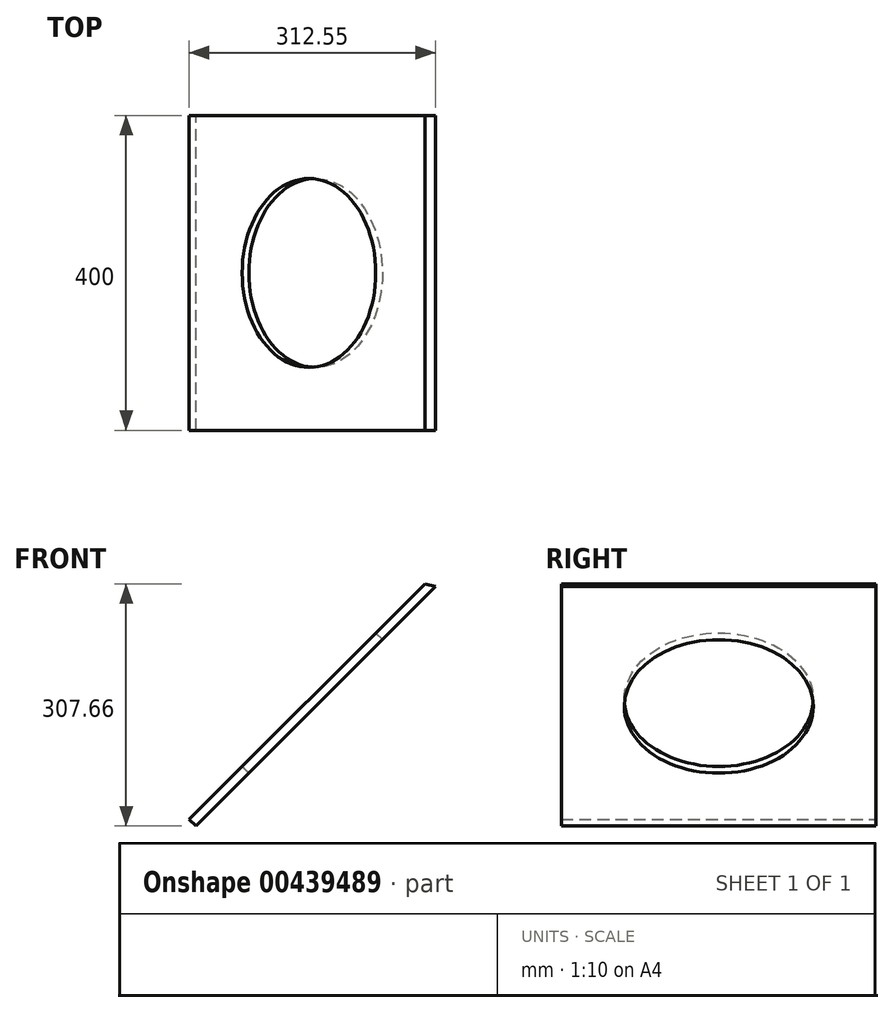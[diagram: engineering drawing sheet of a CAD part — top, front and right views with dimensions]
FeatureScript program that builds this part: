
annotation { "Feature Type Name" : "Feature", "Feature Type Description" : "" }
export const myFeature = defineFeature(function(context is Context, id is Id, definition is map)
    precondition{}
    {
        {
            var Q0;
            Q0=qCreatedBy(makeId("Front.planeOp"),FACE);
            var sketch = newSketch(context, id + "F0", { "sketchPlane" : qUnion([Q0])});
            skLineSegment(sketch, "E0", {"start": v(127.44, -185) * mm, "end": v(-278.86, -185) * mm, "construction": true});
            skLineSegment(sketch, "E1", {"start": v(-278.86, -185) * mm, "end": v(-278.86, 66.39) * mm, "construction": true});
            skLineSegment(sketch, "E2", {"start": v(-274.47, 77) * mm, "end": v(19.17, 370.63) * mm, "construction": true});
            skLineSegment(sketch, "E3", {"start": v(28.83, 373.21) * mm, "end": v(116.32, 349.77) * mm, "construction": true});
            skLineSegment(sketch, "E4", {"start": v(127.44, 335.28) * mm, "end": v(127.44, -185) * mm, "construction": true});
            skLineSegment(sketch, "E5", {"start": v(-273.86, -175) * mm, "end": v(-273.86, 61.28) * mm, "construction": true});
            skLineSegment(sketch, "E6", {"start": v(-278.86, 63.36) * mm, "end": v(25.2, 367.42) * mm, "construction": true});
            skLineSegment(sketch, "E7", {"start": v(25.2, 367.42) * mm, "end": v(120.9, 341.78) * mm, "construction": true});
            skLineSegment(sketch, "E8", {"start": v(112, 331.74) * mm, "end": v(112, -55) * mm, "construction": true});
            skLineSegment(sketch, "E9", {"start": v(100, -167) * mm, "end": v(-261.86, -167) * mm, "construction": true});
            skLineSegment(sketch, "E10", {"start": v(100, -167) * mm, "end": v(100, -185) * mm, "construction": true});
            skLineSegment(sketch, "E11", {"start": v(-261.86, -167) * mm, "end": v(-261.86, -175) * mm, "construction": true});
            skLineSegment(sketch, "E12", {"start": v(-261.86, -175) * mm, "end": v(-273.86, -175) * mm, "construction": true});
            skLineSegment(sketch, "E13", {"start": v(120.9, 341.78) * mm, "end": v(117.8, 330.19) * mm, "construction": true});
            skLineSegment(sketch, "E14", {"start": v(117.8, 330.19) * mm, "end": v(112, 331.74) * mm, "construction": true});
            skLineSegment(sketch, "E15", {"start": v(-273.86, 61.28) * mm, "end": v(20.98, 356.13) * mm, "construction": true});
            skLineSegment(sketch, "E16", {"start": v(112, 331.74) * mm, "end": v(15.4, 357.62) * mm});
            skPoint(sketch, "E17.visualSharp", {"position": v(-278.86, 72.6) * mm});
            skArc(sketch, "E17.filletArc", {"start": v(-274.47, 77) * mm, "mid": v(-277.72, 72.13) * mm, "end": v(-278.86, 66.39) * mm, "construction": true});
            skPoint(sketch, "E18.visualSharp", {"position": v(23.25, 374.7) * mm});
            skArc(sketch, "E18.filletArc", {"start": v(28.83, 373.21) * mm, "mid": v(23.65, 373.21) * mm, "end": v(19.17, 370.63) * mm, "construction": true});
            skPoint(sketch, "E19.visualSharp", {"position": v(127.44, 346.8) * mm});
            skArc(sketch, "E19.filletArc", {"start": v(127.44, 335.28) * mm, "mid": v(124.34, 344.41) * mm, "end": v(116.32, 349.77) * mm, "construction": true});
            skLineSegment(sketch, "E20", {"start": v(23.65, 373.21) * mm, "end": v(26.24, 363.56) * mm, "construction": true});
            skLineSegment(sketch, "E21.left", {"start": v(50, 24) * mm, "end": v(50, 70) * mm, "construction": true});
            skLineSegment(sketch, "E21.right", {"start": v(-50, 24) * mm, "end": v(-50, 70) * mm, "construction": true});
            skPoint(sketch, "E21.middle", {"position": v(0, 0) * mm});
            skArc(sketch, "E22.filletArc", {"start": v(-35, 85) * mm, "mid": v(-45.6, 80.6) * mm, "end": v(-50, 70) * mm, "construction": true});
            skArc(sketch, "E23.filletArc", {"start": v(50, 70) * mm, "mid": v(45.6, 80.6) * mm, "end": v(35, 85) * mm, "construction": true});
            skLineSegment(sketch, "E24", {"start": v(-261.86, 73.28) * mm, "end": v(-233.57, 45) * mm, "construction": true});
            skLineSegment(sketch, "E25", {"start": v(-233.57, 45) * mm, "end": v(65.6, 344.17) * mm});
            skLineSegment(sketch, "E26", {"start": v(112.44, 335.28) * mm, "end": v(124.34, 344.41) * mm, "construction": true});
            skLineSegment(sketch, "E27", {"start": v(100, -155) * mm, "end": v(100, -67) * mm, "construction": true});
            skLineSegment(sketch, "E28", {"start": v(100, -55) * mm, "end": v(88, -55) * mm, "construction": true});
            skLineSegment(sketch, "E29", {"start": v(88, -55) * mm, "end": v(88, -155) * mm, "construction": true});
            skLineSegment(sketch, "E30", {"start": v(88, -155) * mm, "end": v(100, -155) * mm, "construction": true});
            skLineSegment(sketch, "E31", {"start": v(100, -55) * mm, "end": v(100, 334.95) * mm, "construction": true});
            skLineSegment(sketch, "E32", {"start": v(-82, -155) * mm, "end": v(-261.86, -155) * mm, "construction": true});
            skLineSegment(sketch, "E33", {"start": v(-82, -155) * mm, "end": v(88, -155) * mm, "construction": true});
            skLineSegment(sketch, "E34", {"start": v(-82, -155) * mm, "end": v(-82, 25) * mm, "construction": true});
            skLineSegment(sketch, "E35", {"start": v(88, 25) * mm, "end": v(-82, 25) * mm, "construction": true});
            skLineSegment(sketch, "E36", {"start": v(88, -55) * mm, "end": v(88, 25) * mm, "construction": true});
            skLineSegment(sketch, "E37", {"start": v(-50, 24) * mm, "end": v(-55, 24) * mm, "construction": true});
            skLineSegment(sketch, "E38", {"start": v(55, 24) * mm, "end": v(50, 24) * mm, "construction": true});
            skLineSegment(sketch, "E39", {"start": v(-55, 24) * mm, "end": v(-55, 194) * mm, "construction": true});
            skLineSegment(sketch, "E40", {"start": v(55, 194) * mm, "end": v(55, 24) * mm, "construction": true});
            skLineSegment(sketch, "E41", {"start": v(127.44, -55) * mm, "end": v(-261.86, -55) * mm, "construction": true});
            skLineSegment(sketch, "E42", {"start": v(-261.86, -55) * mm, "end": v(-261.86, -67) * mm, "construction": true});
            skLineSegment(sketch, "E43", {"start": v(-261.86, -67) * mm, "end": v(88, -67) * mm, "construction": true});
            skLineSegment(sketch, "E44", {"start": v(127.44, -67) * mm, "end": v(127.44, -55) * mm});
            skLineSegment(sketch, "E45", {"start": v(100, -67) * mm, "end": v(100, -55) * mm, "construction": true});
            skLineSegment(sketch, "E46", {"start": v(88, -67) * mm, "end": v(127.44, -67) * mm, "construction": true});
            skLineSegment(sketch, "E47", {"start": v(112, -67) * mm, "end": v(112, -185) * mm, "construction": true});
            skLineSegment(sketch, "E48", {"start": v(112, -55) * mm, "end": v(112, -67) * mm, "construction": true});
            skLineSegment(sketch, "E49", {"start": v(-261.86, -55) * mm, "end": v(-261.86, -55) * mm});
            skLineSegment(sketch, "E50", {"start": v(-261.86, -55) * mm, "end": v(-261.86, 73.28) * mm, "construction": true});
            skLineSegment(sketch, "E51", {"start": v(-273.86, 61.28) * mm, "end": v(-278.86, 56.28) * mm, "construction": true});
            skLineSegment(sketch, "E52", {"start": v(-233.57, 45) * mm, "end": v(-225.09, 36.51) * mm});
            skLineSegment(sketch, "E53", {"start": v(-225.09, 36.51) * mm, "end": v(78.98, 340.59) * mm});
            skArc(sketch, "E54", {"start": v(-35, 85) * mm, "mid": v(0, 80.55) * mm, "end": v(35, 85) * mm, "construction": true});
            skLineSegment(sketch, "E55", {"start": v(-55, 194) * mm, "end": v(-67, 194) * mm, "construction": true});
            skLineSegment(sketch, "E56", {"start": v(-67, 194) * mm, "end": v(-67, 0) * mm, "construction": true});
            skLineSegment(sketch, "E57", {"start": v(55, 194) * mm, "end": v(67, 194) * mm, "construction": true});
            skLineSegment(sketch, "E58", {"start": v(-50, 24) * mm, "end": v(-50, 0) * mm, "construction": true});
            skLineSegment(sketch, "E59", {"start": v(-50, 0) * mm, "end": v(-67, 0) * mm, "construction": true});
            skLineSegment(sketch, "E60", {"start": v(50, 24) * mm, "end": v(50, 0) * mm, "construction": true});
            skLineSegment(sketch, "E61", {"start": v(-50, 0) * mm, "end": v(50, 0) * mm, "construction": true});
            skLineSegment(sketch, "E62", {"start": v(67, 194) * mm, "end": v(67, 0) * mm, "construction": true});
            skLineSegment(sketch, "E63", {"start": v(67, 0) * mm, "end": v(50, 0) * mm, "construction": true});
            skLineSegment(sketch, "E64", {"start": v(-55, 194) * mm, "end": v(55, 194) * mm, "construction": true});
            skLineSegment(sketch, "E65", {"start": v(-55, 182) * mm, "end": v(55, 182) * mm, "construction": true});
            skLineSegment(sketch, "E66", {"start": v(100, -167) * mm, "end": v(100, -167) * mm});
            skLineSegment(sketch, "E67", {"start": v(100, -155) * mm, "end": v(100, -155) * mm});
            skLineSegment(sketch, "E68", {"start": v(-261.86, -155) * mm, "end": v(-261.86, -67) * mm, "construction": true});
            skLineSegment(sketch, "E69", {"start": v(-261.86, -155) * mm, "end": v(-265.86, -155) * mm, "construction": true});
            skLineSegment(sketch, "E70", {"start": v(-265.86, -155) * mm, "end": v(-265.86, -167) * mm, "construction": true});
            skLineSegment(sketch, "E71", {"start": v(-265.86, -167) * mm, "end": v(-261.86, -167) * mm, "construction": true});
            skLineSegment(sketch, "E72", {"start": v(100, -155) * mm, "end": v(100, -167) * mm, "construction": true});
            skSolve(sketch);
        }
        {
            var Q0;
            Q0 = qSketchRegion(id + "F0", true);
            extrude(context, id + "F1", {"entities" : qUnion([Q0]), "depth" : 400 * mm, "offsetDistance" : 25 * mm});
        }
        {
            var Q0;
            Q0=makeQuery(id+"F1.opExtrude","SWEPT_FACE",FACE,{"disambiguationData":[OSD([sQuery(id+"F0.wireOp",EDGE,"E53")])]});
            var sketch = newSketch(context, id + "F2", { "sketchPlane" : qUnion([Q0])});
            skLineSegment(sketch, "E73", {"start": v(-400, 81.67) * mm, "end": v(0, 81.67) * mm});
            skCircle(sketch, "E74", {"center": v(-200, 81.67) * mm, "radius": 120 * mm});
            skSolve(sketch);
        }
        {
            var Q0;
            {var subQ0=sQuery(id+"F2.wireOp",EDGE,"E74");var subQ1=sQuery(id+"F2.wireOp",EDGE,"E73");var subQ2=makeQuery(id+"F2.imprint","INTERSECT",VERTEX,{"disambiguationData":[OD(0.0)],"derivedFrom":[subQ1,subQ0]});Q0=makeQuery(id+"F2.imprint","IMPRINT",FACE,{"disambiguationData":[TD([[makeQuery(id+"F2.imprint","IMPRINT",EDGE,{"disambiguationData":[TD([[subQ2,-1.0]])],"derivedFrom":subQ1}),-1.0]])]});}
            var Q1;
            {var subQ0=sQuery(id+"F2.wireOp",EDGE,"E74");var subQ1=sQuery(id+"F2.wireOp",EDGE,"E73");var subQ2=makeQuery(id+"F2.imprint","INTERSECT",VERTEX,{"disambiguationData":[OD(0.0)],"derivedFrom":[subQ1,subQ0]});Q1=makeQuery(id+"F2.imprint","IMPRINT",FACE,{"disambiguationData":[TD([[makeQuery(id+"F2.imprint","IMPRINT",EDGE,{"disambiguationData":[TD([[subQ2,-1.0]])],"derivedFrom":subQ1}),1.0]])]});}
            extrude(context, id + "F3", {"entities" : qUnion([Q0, Q1]), "operationType" : NewBodyOperationType.REMOVE, "oppositeDirection" : true, "depth" : 25 * mm, "offsetDistance" : 25 * mm});
        }
    });
